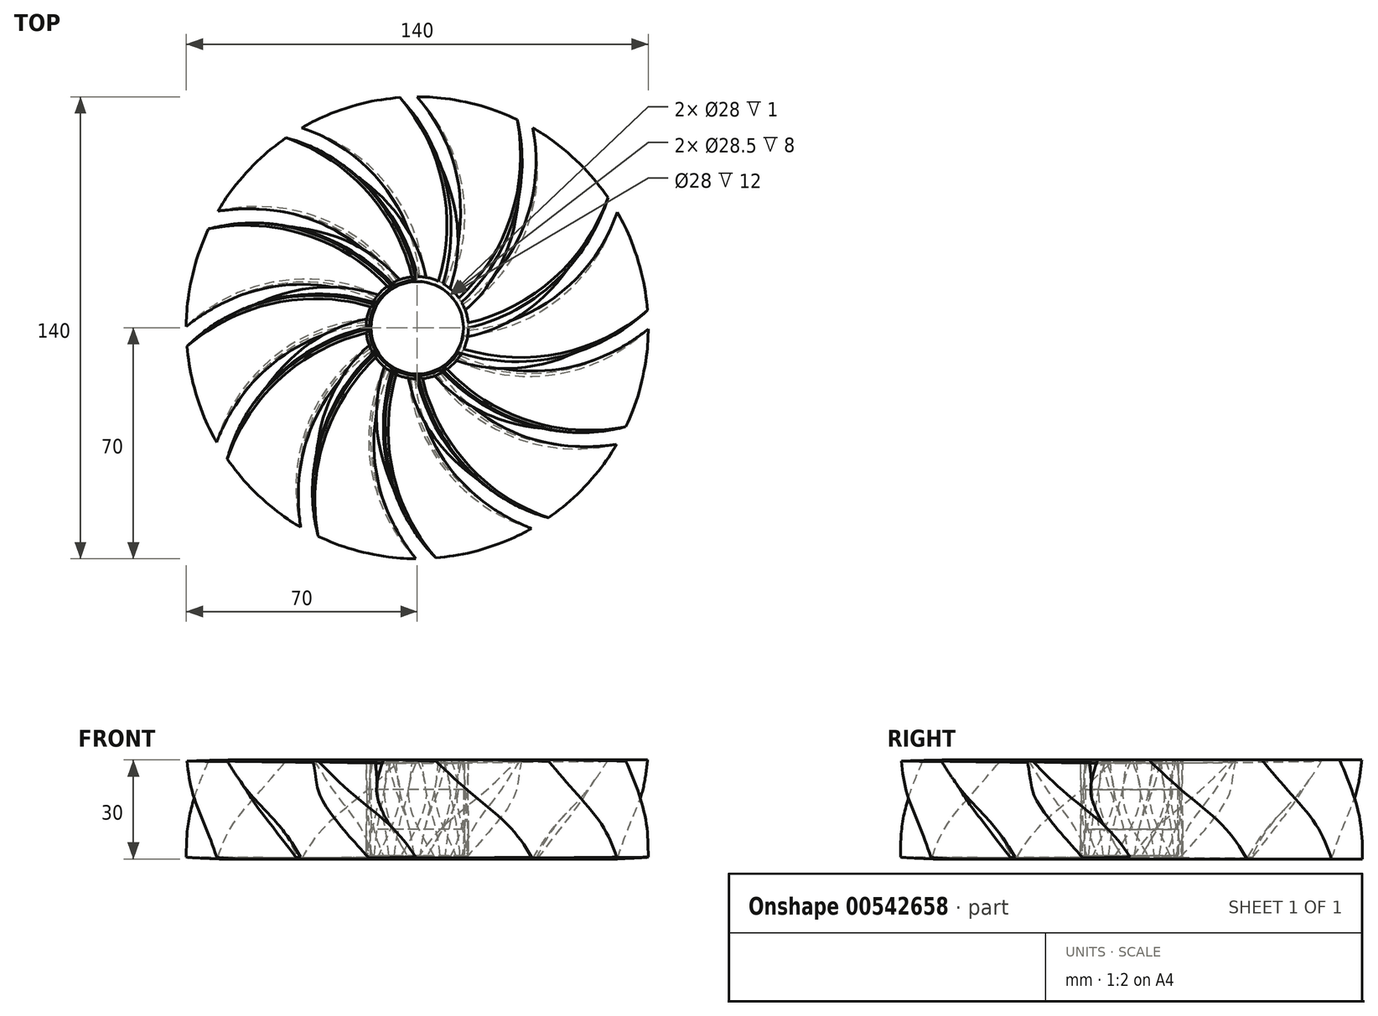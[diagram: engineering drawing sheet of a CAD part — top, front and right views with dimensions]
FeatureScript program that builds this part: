
annotation { "Feature Type Name" : "Feature", "Feature Type Description" : "" }
export const myFeature = defineFeature(function(context is Context, id is Id, definition is map)
    precondition{}
    {
        {
            var Q0;
            Q0=qCreatedBy(makeId("Top.planeOp"),FACE);
            var sketch = newSketch(context, id + "F0", { "sketchPlane" : qUnion([Q0])});
            skArc(sketch, "E0", {"start": v(0, 0) * mm, "mid": v(35, -13.15) * mm, "end": v(70, 0) * mm});
            skArc(sketch, "E1", {"start": v(0, -2) * mm, "mid": v(35.38, -14.4) * mm, "end": v(70, 0) * mm});
            skLineSegment(sketch, "E2", {"start": v(0, -2) * mm, "end": v(0, 0) * mm});
            skSolve(sketch);
        }
        {
            var Q0;
            Q0=qCreatedBy(makeId("Top.planeOp"),FACE);
            cPlane(context, id + "F1", {"entities" : qUnion([Q0]), "cplaneType" : CPlaneType.OFFSET, "offset" : 10 * mm, "width" : 150 * mm, "height" : 150 * mm});
        }
        {
            var Q0;
            Q0=qCreatedBy(id+"F1.planeOp",FACE);
            var sketch = newSketch(context, id + "F2", { "sketchPlane" : qUnion([Q0])});
            skArc(sketch, "E3", {"start": v(0, 0) * mm, "mid": v(33.25, -17.1) * mm, "end": v(69.54, -8.05) * mm});
            skArc(sketch, "E4", {"start": v(-0.44, -4.98) * mm, "mid": v(33.82, -23.17) * mm, "end": v(69.54, -8.05) * mm});
            skLineSegment(sketch, "E5", {"start": v(-0.44, -4.98) * mm, "end": v(0, 0) * mm});
            skSolve(sketch);
        }
        {
            var Q0;
            Q0=qCreatedBy(id+"F1.planeOp",FACE);
            cPlane(context, id + "F3", {"entities" : qUnion([Q0]), "cplaneType" : CPlaneType.OFFSET, "offset" : 10 * mm, "width" : 150 * mm, "height" : 150 * mm});
        }
        {
            var Q0;
            Q0=qCreatedBy(id+"F3.planeOp",FACE);
            var sketch = newSketch(context, id + "F4", { "sketchPlane" : qUnion([Q0])});
            skArc(sketch, "E6", {"start": v(0, 0) * mm, "mid": v(29.78, -22.6) * mm, "end": v(67.08, -20) * mm});
            skArc(sketch, "E7", {"start": v(-1.3, -4.83) * mm, "mid": v(29.28, -28.7) * mm, "end": v(67.08, -20) * mm});
            skLineSegment(sketch, "E8", {"start": v(-1.3, -4.83) * mm, "end": v(0, 0) * mm});
            skSolve(sketch);
        }
        {
            var Q0;
            Q0=qCreatedBy(id+"F3.planeOp",FACE);
            cPlane(context, id + "F5", {"entities" : qUnion([Q0]), "cplaneType" : CPlaneType.OFFSET, "offset" : 10 * mm, "width" : 150 * mm, "height" : 150 * mm});
        }
        {
            var Q0;
            Q0=qCreatedBy(id+"F5.planeOp",FACE);
            var sketch = newSketch(context, id + "F6", { "sketchPlane" : qUnion([Q0])});
            skArc(sketch, "E9", {"start": v(0, 0) * mm, "mid": v(26.56, -25.53) * mm, "end": v(63.1, -30.32) * mm});
            skArc(sketch, "E10", {"start": v(-0.85, -1.81) * mm, "mid": v(26.37, -26.72) * mm, "end": v(63.1, -30.32) * mm});
            skLineSegment(sketch, "E11", {"start": v(-0.85, -1.81) * mm, "end": v(0, 0) * mm});
            skSolve(sketch);
        }
        {
            var Q0;
            Q0=makeQuery(id+"F0.imprint","IMPRINT",FACE,{"disambiguationData":[TD([[makeQuery(id+"F0.imprint","IMPRINT",EDGE,{"derivedFrom":sQuery(id+"F0.wireOp",EDGE,"E0")}),-1.0]])]});
            var Q1;
            Q1=makeQuery(id+"F2.imprint","IMPRINT",FACE,{"disambiguationData":[TD([[makeQuery(id+"F2.imprint","IMPRINT",EDGE,{"derivedFrom":sQuery(id+"F2.wireOp",EDGE,"E3")}),-1.0]])]});
            var Q2;
            Q2=makeQuery(id+"F4.imprint","IMPRINT",FACE,{"disambiguationData":[TD([[makeQuery(id+"F4.imprint","IMPRINT",EDGE,{"derivedFrom":sQuery(id+"F4.wireOp",EDGE,"E6")}),-1.0]])]});
            var Q3;
            Q3=makeQuery(id+"F6.imprint","IMPRINT",FACE,{"disambiguationData":[TD([[makeQuery(id+"F6.imprint","IMPRINT",EDGE,{"derivedFrom":sQuery(id+"F6.wireOp",EDGE,"E9")}),-1.0]])]});
            loft(context, id + "F7", {"sheetProfilesArray" : [{ "sheetProfileEntities" : qUnion([Q0]) }, { "sheetProfileEntities" : qUnion([Q1]) }, { "sheetProfileEntities" : qUnion([Q2]) }, { "sheetProfileEntities" : qUnion([Q3]) }]});
        }
        {
            var Q0;
            Q0=qCreatedBy(makeId("Top.planeOp"),FACE);
            var sketch = newSketch(context, id + "F8", { "sketchPlane" : qUnion([Q0])});
            skLineSegment(sketch, "E12", {"start": v(0, 0) * mm, "end": v(-0.34, -0.76) * mm});
            skLineSegment(sketch, "E13", {"start": v(-0.34, -0.76) * mm, "end": v(0.32, -0.76) * mm});
            skLineSegment(sketch, "E14", {"start": v(0.32, -0.76) * mm, "end": v(0, 0) * mm});
            skSolve(sketch);
        }
        {
            var Q0;
            Q0 = qSketchRegion(id + "F8", true);
            extrude(context, id + "F9", {"entities" : qUnion([Q0]), "operationType" : NewBodyOperationType.ADD, "depth" : 40 * mm, "offsetDistance" : 25 * mm});
        }
        {
            var Q0;
            Q0=makeQuery(id+"F7.opLoft","SWEPT_BODY",BODY,{"disambiguationData":[OSD([makeQuery(id+"F0.imprint","IMPRINT",FACE,{"disambiguationData":[TD([[makeQuery(id+"F0.imprint","IMPRINT",EDGE,{"derivedFrom":sQuery(id+"F0.wireOp",EDGE,"E0")}),-1.0]])]}),sQuery(id+"F2.wireOp",EDGE,"E5"),sQuery(id+"F4.wireOp",EDGE,"E8"),makeQuery(id+"F6.imprint","IMPRINT",FACE,{"disambiguationData":[TD([[makeQuery(id+"F6.imprint","IMPRINT",EDGE,{"derivedFrom":sQuery(id+"F6.wireOp",EDGE,"E9")}),-1.0]])]})])]});
            var Q1;
            Q1=makeQuery(id+"F9.boolean.opBoolean","SPLIT",EDGE,{"derivedFrom":makeQuery(id+"F9.opExtrude","SWEPT_EDGE",EDGE,{"disambiguationData":[OSD([sQuery(id+"F8.wireOp",EDGE,"E12"),sQuery(id+"F8.wireOp",EDGE,"E14")])]})});
            circularPattern(context, id + "F10", {"entities" : qUnion([Q0]), "axis" : qUnion([Q1]), "angle" : 360 * degree, "instanceCount" : 12, "equalSpace" : true});
        }
        {
            var Q0;
            Q0=qCreatedBy(makeId("Top.planeOp"),FACE);
            var sketch = newSketch(context, id + "F11", { "sketchPlane" : qUnion([Q0])});
            skCircle(sketch, "E15", {"center": v(0, 0) * mm, "radius": 15.5 * mm});
            skSolve(sketch);
        }
        {
            var Q0;
            Q0 = qSketchRegion(id + "F11", true);
            extrude(context, id + "F12", {"entities" : qUnion([Q0]), "operationType" : NewBodyOperationType.ADD, "depth" : 30 * mm, "offsetDistance" : 25 * mm});
        }
        {
            var Q0;
            Q0=qCreatedBy(makeId("Top.planeOp"),FACE);
            var sketch = newSketch(context, id + "F13", { "sketchPlane" : qUnion([Q0])});
            skCircle(sketch, "E16", {"center": v(0, 0) * mm, "radius": 14 * mm});
            skSolve(sketch);
        }
        {
            var Q0;
            Q0 = qSketchRegion(id + "F13", true);
            extrude(context, id + "F14", {"entities" : qUnion([Q0]), "operationType" : NewBodyOperationType.REMOVE, "depth" : 40 * mm, "offsetDistance" : 25 * mm});
        }
        {
            var Q0;
            Q0=qCreatedBy(makeId("Top.planeOp"),FACE);
            var sketch = newSketch(context, id + "F15", { "sketchPlane" : qUnion([Q0])});
            skCircle(sketch, "E17", {"center": v(0, 0) * mm, "radius": 14.25 * mm});
            skSolve(sketch);
        }
        {
            var Q0;
            Q0 = qSketchRegion(id + "F15", true);
            extrude(context, id + "F16", {"entities" : qUnion([Q0]), "operationType" : NewBodyOperationType.REMOVE, "depth" : 9 * mm, "offsetDistance" : 25 * mm, "hasSecondDirection" : true, "secondDirectionOppositeDirection" : false, "secondDirectionDepth" : 1 * mm});
        }
        {
            var Q0;
            Q0 = qSketchRegion(id + "F15", true);
            extrude(context, id + "F17", {"entities" : qUnion([Q0]), "operationType" : NewBodyOperationType.REMOVE, "depth" : 29 * mm, "offsetDistance" : 25 * mm, "hasSecondDirection" : true, "secondDirectionOppositeDirection" : false, "secondDirectionDepth" : 21 * mm});
        }
        {
            var Q0;
            {var subQ0=sQuery(id+"F2.wireOp",EDGE,"E3");var subQ1=sQuery(id+"F2.wireOp",EDGE,"E4");var subQ2=makeQuery(id+"F2.imprint","INTERSECT",VERTEX,{"derivedFrom":[subQ0,subQ1]});var subQ3=sQuery(id+"F2.wireOp",EDGE,"E5");var subQ4=sQuery(id+"F0.wireOp",EDGE,"E0");var subQ5=sQuery(id+"F0.wireOp",EDGE,"E1");var subQ6=makeQuery(id+"F0.imprint","INTERSECT",VERTEX,{"derivedFrom":[subQ4,subQ5]});var subQ7=sQuery(id+"F0.wireOp",EDGE,"E2");var subQ10=sQuery(id+"F11.wireOp",EDGE,"E15");Q0=makeQuery(id+"F12.boolean.opBoolean","SPLIT",EDGE,{"disambiguationData":[TD([makeQuery(id+"F10.opPattern","COPY",FACE,{"derivedFrom":makeQuery(id+"F7.opLoft","SWEPT_FACE",FACE,{"disambiguationData":[OSD([subQ4,subQ5,subQ7,subQ0,subQ1,subQ3]),TDD([subQ6,makeQuery(id+"F0.imprint","INTERSECT",VERTEX,{"derivedFrom":[subQ5,subQ7]}),makeQuery(id+"F0.imprint","IMPRINT",EDGE,{"derivedFrom":subQ5}),subQ2,makeQuery(id+"F2.imprint","INTERSECT",VERTEX,{"derivedFrom":[subQ1,subQ3]}),makeQuery(id+"F2.imprint","IMPRINT",EDGE,{"derivedFrom":subQ1})])]}),"instanceName":"3"})])],"derivedFrom":makeQuery(id+"F12.opExtrude","CAP_EDGE",EDGE,{"disambiguationData":[OSD([subQ10])],"isStart":false})});}
            var Q1;
            {var subQ0=sQuery(id+"F2.wireOp",EDGE,"E3");var subQ1=sQuery(id+"F2.wireOp",EDGE,"E4");var subQ2=makeQuery(id+"F2.imprint","INTERSECT",VERTEX,{"derivedFrom":[subQ0,subQ1]});var subQ3=sQuery(id+"F2.wireOp",EDGE,"E5");var subQ4=sQuery(id+"F0.wireOp",EDGE,"E0");var subQ5=sQuery(id+"F0.wireOp",EDGE,"E1");var subQ6=makeQuery(id+"F0.imprint","INTERSECT",VERTEX,{"derivedFrom":[subQ4,subQ5]});var subQ7=sQuery(id+"F0.wireOp",EDGE,"E2");var subQ10=sQuery(id+"F11.wireOp",EDGE,"E15");Q1=makeQuery(id+"F12.boolean.opBoolean","SPLIT",EDGE,{"disambiguationData":[TD([makeQuery(id+"F10.opPattern","COPY",FACE,{"derivedFrom":makeQuery(id+"F7.opLoft","SWEPT_FACE",FACE,{"disambiguationData":[OSD([subQ4,subQ5,subQ7,subQ0,subQ1,subQ3]),TDD([subQ6,makeQuery(id+"F0.imprint","INTERSECT",VERTEX,{"derivedFrom":[subQ5,subQ7]}),makeQuery(id+"F0.imprint","IMPRINT",EDGE,{"derivedFrom":subQ5}),subQ2,makeQuery(id+"F2.imprint","INTERSECT",VERTEX,{"derivedFrom":[subQ1,subQ3]}),makeQuery(id+"F2.imprint","IMPRINT",EDGE,{"derivedFrom":subQ1})])]}),"instanceName":"4"})])],"derivedFrom":makeQuery(id+"F12.opExtrude","CAP_EDGE",EDGE,{"disambiguationData":[OSD([subQ10])],"isStart":false})});}
            var Q2;
            {var subQ0=sQuery(id+"F2.wireOp",EDGE,"E3");var subQ1=sQuery(id+"F2.wireOp",EDGE,"E4");var subQ2=makeQuery(id+"F2.imprint","INTERSECT",VERTEX,{"derivedFrom":[subQ0,subQ1]});var subQ3=sQuery(id+"F2.wireOp",EDGE,"E5");var subQ4=sQuery(id+"F0.wireOp",EDGE,"E0");var subQ5=sQuery(id+"F0.wireOp",EDGE,"E1");var subQ6=makeQuery(id+"F0.imprint","INTERSECT",VERTEX,{"derivedFrom":[subQ4,subQ5]});var subQ7=sQuery(id+"F0.wireOp",EDGE,"E2");var subQ10=sQuery(id+"F11.wireOp",EDGE,"E15");Q2=makeQuery(id+"F12.boolean.opBoolean","SPLIT",EDGE,{"disambiguationData":[TD([makeQuery(id+"F10.opPattern","COPY",FACE,{"derivedFrom":makeQuery(id+"F7.opLoft","SWEPT_FACE",FACE,{"disambiguationData":[OSD([subQ4,subQ5,subQ7,subQ0,subQ1,subQ3]),TDD([subQ6,makeQuery(id+"F0.imprint","INTERSECT",VERTEX,{"derivedFrom":[subQ5,subQ7]}),makeQuery(id+"F0.imprint","IMPRINT",EDGE,{"derivedFrom":subQ5}),subQ2,makeQuery(id+"F2.imprint","INTERSECT",VERTEX,{"derivedFrom":[subQ1,subQ3]}),makeQuery(id+"F2.imprint","IMPRINT",EDGE,{"derivedFrom":subQ1})])]}),"instanceName":"5"})])],"derivedFrom":makeQuery(id+"F12.opExtrude","CAP_EDGE",EDGE,{"disambiguationData":[OSD([subQ10])],"isStart":false})});}
            var Q3;
            {var subQ0=sQuery(id+"F2.wireOp",EDGE,"E3");var subQ1=sQuery(id+"F2.wireOp",EDGE,"E4");var subQ2=makeQuery(id+"F2.imprint","INTERSECT",VERTEX,{"derivedFrom":[subQ0,subQ1]});var subQ3=sQuery(id+"F2.wireOp",EDGE,"E5");var subQ4=sQuery(id+"F0.wireOp",EDGE,"E0");var subQ5=sQuery(id+"F0.wireOp",EDGE,"E1");var subQ6=makeQuery(id+"F0.imprint","INTERSECT",VERTEX,{"derivedFrom":[subQ4,subQ5]});var subQ7=sQuery(id+"F0.wireOp",EDGE,"E2");var subQ10=sQuery(id+"F11.wireOp",EDGE,"E15");Q3=makeQuery(id+"F12.boolean.opBoolean","SPLIT",EDGE,{"disambiguationData":[TD([makeQuery(id+"F10.opPattern","COPY",FACE,{"derivedFrom":makeQuery(id+"F7.opLoft","SWEPT_FACE",FACE,{"disambiguationData":[OSD([subQ4,subQ5,subQ7,subQ0,subQ1,subQ3]),TDD([subQ6,makeQuery(id+"F0.imprint","INTERSECT",VERTEX,{"derivedFrom":[subQ5,subQ7]}),makeQuery(id+"F0.imprint","IMPRINT",EDGE,{"derivedFrom":subQ5}),subQ2,makeQuery(id+"F2.imprint","INTERSECT",VERTEX,{"derivedFrom":[subQ1,subQ3]}),makeQuery(id+"F2.imprint","IMPRINT",EDGE,{"derivedFrom":subQ1})])]}),"instanceName":"6"})])],"derivedFrom":makeQuery(id+"F12.opExtrude","CAP_EDGE",EDGE,{"disambiguationData":[OSD([subQ10])],"isStart":false})});}
            var Q4;
            {var subQ0=sQuery(id+"F2.wireOp",EDGE,"E4");var subQ1=sQuery(id+"F2.wireOp",EDGE,"E5");var subQ2=sQuery(id+"F2.wireOp",EDGE,"E3");var subQ3=makeQuery(id+"F2.imprint","INTERSECT",VERTEX,{"derivedFrom":[subQ2,subQ0]});var subQ4=sQuery(id+"F0.wireOp",EDGE,"E1");var subQ5=sQuery(id+"F0.wireOp",EDGE,"E2");var subQ6=sQuery(id+"F0.wireOp",EDGE,"E0");var subQ7=makeQuery(id+"F0.imprint","INTERSECT",VERTEX,{"derivedFrom":[subQ6,subQ4]});var subQ10=sQuery(id+"F11.wireOp",EDGE,"E15");Q4=makeQuery(id+"F12.boolean.opBoolean","SPLIT",EDGE,{"disambiguationData":[TD([makeQuery(id+"F7.opLoft","SWEPT_FACE",FACE,{"disambiguationData":[OSD([subQ6,subQ4,subQ5,subQ2,subQ0,subQ1]),TDD([makeQuery(id+"F0.imprint","INTERSECT",VERTEX,{"derivedFrom":[subQ6,subQ5]}),subQ7,makeQuery(id+"F0.imprint","IMPRINT",EDGE,{"derivedFrom":subQ6}),makeQuery(id+"F2.imprint","INTERSECT",VERTEX,{"derivedFrom":[subQ2,subQ1]}),subQ3,makeQuery(id+"F2.imprint","IMPRINT",EDGE,{"derivedFrom":subQ2})])]})])],"derivedFrom":makeQuery(id+"F12.opExtrude","CAP_EDGE",EDGE,{"disambiguationData":[OSD([subQ10])],"isStart":false})});}
            var Q5;
            {var subQ0=sQuery(id+"F2.wireOp",EDGE,"E4");var subQ1=sQuery(id+"F2.wireOp",EDGE,"E5");var subQ2=sQuery(id+"F2.wireOp",EDGE,"E3");var subQ3=makeQuery(id+"F2.imprint","INTERSECT",VERTEX,{"derivedFrom":[subQ2,subQ0]});var subQ4=sQuery(id+"F0.wireOp",EDGE,"E1");var subQ5=sQuery(id+"F0.wireOp",EDGE,"E2");var subQ6=sQuery(id+"F0.wireOp",EDGE,"E0");var subQ7=makeQuery(id+"F0.imprint","INTERSECT",VERTEX,{"derivedFrom":[subQ6,subQ4]});var subQ10=sQuery(id+"F11.wireOp",EDGE,"E15");Q5=makeQuery(id+"F12.boolean.opBoolean","SPLIT",EDGE,{"disambiguationData":[TD([makeQuery(id+"F7.opLoft","SWEPT_FACE",FACE,{"disambiguationData":[OSD([subQ6,subQ4,subQ5,subQ2,subQ0,subQ1]),TDD([subQ7,makeQuery(id+"F0.imprint","INTERSECT",VERTEX,{"derivedFrom":[subQ4,subQ5]}),makeQuery(id+"F0.imprint","IMPRINT",EDGE,{"derivedFrom":subQ4}),subQ3,makeQuery(id+"F2.imprint","INTERSECT",VERTEX,{"derivedFrom":[subQ0,subQ1]}),makeQuery(id+"F2.imprint","IMPRINT",EDGE,{"derivedFrom":subQ0})])]})])],"derivedFrom":makeQuery(id+"F12.opExtrude","CAP_EDGE",EDGE,{"disambiguationData":[OSD([subQ10])],"isStart":false})});}
            var Q6;
            {var subQ2=sQuery(id+"F2.wireOp",EDGE,"E4");var subQ3=sQuery(id+"F2.wireOp",EDGE,"E5");var subQ4=sQuery(id+"F2.wireOp",EDGE,"E3");var subQ5=makeQuery(id+"F2.imprint","INTERSECT",VERTEX,{"derivedFrom":[subQ4,subQ2]});var subQ6=sQuery(id+"F0.wireOp",EDGE,"E1");var subQ7=sQuery(id+"F0.wireOp",EDGE,"E2");var subQ8=sQuery(id+"F0.wireOp",EDGE,"E0");var subQ9=makeQuery(id+"F0.imprint","INTERSECT",VERTEX,{"derivedFrom":[subQ8,subQ6]});var subQ10=sQuery(id+"F11.wireOp",EDGE,"E15");Q6=makeQuery(id+"F12.boolean.opBoolean","SPLIT",EDGE,{"disambiguationData":[TD([makeQuery(id+"F10.opPattern","COPY",FACE,{"derivedFrom":makeQuery(id+"F7.opLoft","SWEPT_FACE",FACE,{"disambiguationData":[OSD([subQ8,subQ6,subQ7,subQ4,subQ2,subQ3]),TDD([subQ9,makeQuery(id+"F0.imprint","INTERSECT",VERTEX,{"derivedFrom":[subQ6,subQ7]}),makeQuery(id+"F0.imprint","IMPRINT",EDGE,{"derivedFrom":subQ6}),subQ5,makeQuery(id+"F2.imprint","INTERSECT",VERTEX,{"derivedFrom":[subQ2,subQ3]}),makeQuery(id+"F2.imprint","IMPRINT",EDGE,{"derivedFrom":subQ2})])]}),"instanceName":"1"})])],"derivedFrom":makeQuery(id+"F12.opExtrude","CAP_EDGE",EDGE,{"disambiguationData":[OSD([subQ10])],"isStart":false})});}
            var Q7;
            {var subQ0=sQuery(id+"F2.wireOp",EDGE,"E3");var subQ1=sQuery(id+"F2.wireOp",EDGE,"E4");var subQ2=makeQuery(id+"F2.imprint","INTERSECT",VERTEX,{"derivedFrom":[subQ0,subQ1]});var subQ3=sQuery(id+"F2.wireOp",EDGE,"E5");var subQ4=sQuery(id+"F0.wireOp",EDGE,"E0");var subQ5=sQuery(id+"F0.wireOp",EDGE,"E1");var subQ6=makeQuery(id+"F0.imprint","INTERSECT",VERTEX,{"derivedFrom":[subQ4,subQ5]});var subQ7=sQuery(id+"F0.wireOp",EDGE,"E2");var subQ10=sQuery(id+"F11.wireOp",EDGE,"E15");Q7=makeQuery(id+"F12.boolean.opBoolean","SPLIT",EDGE,{"disambiguationData":[TD([makeQuery(id+"F10.opPattern","COPY",FACE,{"derivedFrom":makeQuery(id+"F7.opLoft","SWEPT_FACE",FACE,{"disambiguationData":[OSD([subQ4,subQ5,subQ7,subQ0,subQ1,subQ3]),TDD([subQ6,makeQuery(id+"F0.imprint","INTERSECT",VERTEX,{"derivedFrom":[subQ5,subQ7]}),makeQuery(id+"F0.imprint","IMPRINT",EDGE,{"derivedFrom":subQ5}),subQ2,makeQuery(id+"F2.imprint","INTERSECT",VERTEX,{"derivedFrom":[subQ1,subQ3]}),makeQuery(id+"F2.imprint","IMPRINT",EDGE,{"derivedFrom":subQ1})])]}),"instanceName":"2"})])],"derivedFrom":makeQuery(id+"F12.opExtrude","CAP_EDGE",EDGE,{"disambiguationData":[OSD([subQ10])],"isStart":false})});}
            var Q8;
            {var subQ0=sQuery(id+"F6.wireOp",EDGE,"E9");var subQ1=sQuery(id+"F6.wireOp",EDGE,"E10");var subQ2=sQuery(id+"F6.wireOp",EDGE,"E11");Q8=makeQuery(id+"F10.opPattern","COPY",EDGE,{"derivedFrom":makeQuery(id+"F7.opLoft","MID_CAP_EDGE",EDGE,{"disambiguationData":[OSD([subQ0,subQ1,subQ2]),TDD([makeQuery(id+"F6.imprint","INTERSECT",VERTEX,{"derivedFrom":[subQ0,subQ2]}),makeQuery(id+"F6.imprint","INTERSECT",VERTEX,{"derivedFrom":[subQ0,subQ1]}),makeQuery(id+"F6.imprint","IMPRINT",EDGE,{"derivedFrom":subQ0})])],"capPos":3.0}),"instanceName":"5"});}
            var Q9;
            {var subQ0=sQuery(id+"F6.wireOp",EDGE,"E9");var subQ1=sQuery(id+"F6.wireOp",EDGE,"E10");var subQ2=sQuery(id+"F6.wireOp",EDGE,"E11");Q9=makeQuery(id+"F10.opPattern","COPY",EDGE,{"derivedFrom":makeQuery(id+"F7.opLoft","MID_CAP_EDGE",EDGE,{"disambiguationData":[OSD([subQ0,subQ1,subQ2]),TDD([makeQuery(id+"F6.imprint","INTERSECT",VERTEX,{"derivedFrom":[subQ0,subQ2]}),makeQuery(id+"F6.imprint","INTERSECT",VERTEX,{"derivedFrom":[subQ0,subQ1]}),makeQuery(id+"F6.imprint","IMPRINT",EDGE,{"derivedFrom":subQ0})])],"capPos":3.0}),"instanceName":"4"});}
            var Q10;
            {var subQ0=sQuery(id+"F6.wireOp",EDGE,"E9");var subQ1=sQuery(id+"F6.wireOp",EDGE,"E10");var subQ2=sQuery(id+"F6.wireOp",EDGE,"E11");Q10=makeQuery(id+"F10.opPattern","COPY",EDGE,{"derivedFrom":makeQuery(id+"F7.opLoft","MID_CAP_EDGE",EDGE,{"disambiguationData":[OSD([subQ0,subQ1,subQ2]),TDD([makeQuery(id+"F6.imprint","INTERSECT",VERTEX,{"derivedFrom":[subQ0,subQ2]}),makeQuery(id+"F6.imprint","INTERSECT",VERTEX,{"derivedFrom":[subQ0,subQ1]}),makeQuery(id+"F6.imprint","IMPRINT",EDGE,{"derivedFrom":subQ0})])],"capPos":3.0}),"instanceName":"3"});}
            var Q11;
            {var subQ0=sQuery(id+"F6.wireOp",EDGE,"E9");var subQ1=sQuery(id+"F6.wireOp",EDGE,"E10");var subQ2=sQuery(id+"F6.wireOp",EDGE,"E11");Q11=makeQuery(id+"F10.opPattern","COPY",EDGE,{"derivedFrom":makeQuery(id+"F7.opLoft","MID_CAP_EDGE",EDGE,{"disambiguationData":[OSD([subQ0,subQ1,subQ2]),TDD([makeQuery(id+"F6.imprint","INTERSECT",VERTEX,{"derivedFrom":[subQ0,subQ2]}),makeQuery(id+"F6.imprint","INTERSECT",VERTEX,{"derivedFrom":[subQ0,subQ1]}),makeQuery(id+"F6.imprint","IMPRINT",EDGE,{"derivedFrom":subQ0})])],"capPos":3.0}),"instanceName":"2"});}
            var Q12;
            {var subQ0=sQuery(id+"F6.wireOp",EDGE,"E9");var subQ1=sQuery(id+"F6.wireOp",EDGE,"E10");var subQ2=sQuery(id+"F6.wireOp",EDGE,"E11");Q12=makeQuery(id+"F10.opPattern","COPY",EDGE,{"derivedFrom":makeQuery(id+"F7.opLoft","MID_CAP_EDGE",EDGE,{"disambiguationData":[OSD([subQ0,subQ1,subQ2]),TDD([makeQuery(id+"F6.imprint","INTERSECT",VERTEX,{"derivedFrom":[subQ0,subQ2]}),makeQuery(id+"F6.imprint","INTERSECT",VERTEX,{"derivedFrom":[subQ0,subQ1]}),makeQuery(id+"F6.imprint","IMPRINT",EDGE,{"derivedFrom":subQ0})])],"capPos":3.0}),"instanceName":"1"});}
            var Q13;
            {var subQ0=sQuery(id+"F6.wireOp",EDGE,"E9");var subQ1=sQuery(id+"F6.wireOp",EDGE,"E10");var subQ2=sQuery(id+"F6.wireOp",EDGE,"E11");Q13=makeQuery(id+"F7.opLoft","MID_CAP_EDGE",EDGE,{"disambiguationData":[OSD([subQ0,subQ1,subQ2]),TDD([makeQuery(id+"F6.imprint","INTERSECT",VERTEX,{"derivedFrom":[subQ0,subQ2]}),makeQuery(id+"F6.imprint","INTERSECT",VERTEX,{"derivedFrom":[subQ0,subQ1]}),makeQuery(id+"F6.imprint","IMPRINT",EDGE,{"derivedFrom":subQ0})])],"capPos":3.0});}
            var Q14;
            {var subQ0=sQuery(id+"F6.wireOp",EDGE,"E9");var subQ1=sQuery(id+"F6.wireOp",EDGE,"E10");var subQ2=sQuery(id+"F6.wireOp",EDGE,"E11");Q14=makeQuery(id+"F10.opPattern","COPY",EDGE,{"derivedFrom":makeQuery(id+"F7.opLoft","MID_CAP_EDGE",EDGE,{"disambiguationData":[OSD([subQ0,subQ1,subQ2]),TDD([makeQuery(id+"F6.imprint","INTERSECT",VERTEX,{"derivedFrom":[subQ0,subQ2]}),makeQuery(id+"F6.imprint","INTERSECT",VERTEX,{"derivedFrom":[subQ0,subQ1]}),makeQuery(id+"F6.imprint","IMPRINT",EDGE,{"derivedFrom":subQ0})])],"capPos":3.0}),"instanceName":"7"});}
            var Q15;
            {var subQ0=sQuery(id+"F6.wireOp",EDGE,"E9");var subQ1=sQuery(id+"F6.wireOp",EDGE,"E10");var subQ2=sQuery(id+"F6.wireOp",EDGE,"E11");Q15=makeQuery(id+"F10.opPattern","COPY",EDGE,{"derivedFrom":makeQuery(id+"F7.opLoft","MID_CAP_EDGE",EDGE,{"disambiguationData":[OSD([subQ0,subQ1,subQ2]),TDD([makeQuery(id+"F6.imprint","INTERSECT",VERTEX,{"derivedFrom":[subQ0,subQ2]}),makeQuery(id+"F6.imprint","INTERSECT",VERTEX,{"derivedFrom":[subQ0,subQ1]}),makeQuery(id+"F6.imprint","IMPRINT",EDGE,{"derivedFrom":subQ0})])],"capPos":3.0}),"instanceName":"6"});}
            chamfer(context, id + "F18", {"entities" : qUnion([Q0, Q1, Q2, Q3, Q4, Q5, Q6, Q7, Q8, Q9, Q10, Q11, Q12, Q13, Q14, Q15]), "width" : 1 * mm, "tangentPropagation" : true});
        }
        {
            var Q0;
            {var subQ0=sQuery(id+"F2.wireOp",EDGE,"E3");var subQ1=sQuery(id+"F2.wireOp",EDGE,"E4");var subQ2=makeQuery(id+"F2.imprint","INTERSECT",VERTEX,{"derivedFrom":[subQ0,subQ1]});var subQ3=sQuery(id+"F2.wireOp",EDGE,"E5");var subQ4=sQuery(id+"F0.wireOp",EDGE,"E0");var subQ6=sQuery(id+"F0.wireOp",EDGE,"E1");var subQ7=makeQuery(id+"F0.imprint","INTERSECT",VERTEX,{"derivedFrom":[subQ4,subQ6]});var subQ8=sQuery(id+"F0.wireOp",EDGE,"E2");var subQ9=makeQuery(id+"F0.imprint","IMPRINT",EDGE,{"derivedFrom":subQ6});var subQ11=sQuery(id+"F11.wireOp",EDGE,"E15");Q0=makeQuery(id+"F12.boolean.opBoolean","SPLIT",EDGE,{"disambiguationData":[TD([makeQuery(id+"F10.opPattern","COPY",FACE,{"derivedFrom":makeQuery(id+"F7.opLoft","SWEPT_FACE",FACE,{"disambiguationData":[OSD([subQ4,subQ6,subQ8,subQ0,subQ1,subQ3]),TDD([subQ7,makeQuery(id+"F0.imprint","INTERSECT",VERTEX,{"derivedFrom":[subQ6,subQ8]}),subQ9,subQ2,makeQuery(id+"F2.imprint","INTERSECT",VERTEX,{"derivedFrom":[subQ1,subQ3]}),makeQuery(id+"F2.imprint","IMPRINT",EDGE,{"derivedFrom":subQ1})])]}),"instanceName":"5"})])],"derivedFrom":makeQuery(id+"F12.opExtrude","CAP_EDGE",EDGE,{"disambiguationData":[OSD([subQ11])],"isStart":true})});}
            var Q1;
            {var subQ0=sQuery(id+"F0.wireOp",EDGE,"E1");var subQ1=sQuery(id+"F0.wireOp",EDGE,"E2");var subQ2=sQuery(id+"F0.wireOp",EDGE,"E0");Q1=makeQuery(id+"F10.opPattern","COPY",EDGE,{"derivedFrom":makeQuery(id+"F7.opLoft","MID_CAP_EDGE",EDGE,{"disambiguationData":[OSD([subQ2,subQ0,subQ1]),TDD([makeQuery(id+"F0.imprint","INTERSECT",VERTEX,{"derivedFrom":[subQ2,subQ0]}),makeQuery(id+"F0.imprint","INTERSECT",VERTEX,{"derivedFrom":[subQ0,subQ1]}),makeQuery(id+"F0.imprint","IMPRINT",EDGE,{"derivedFrom":subQ0})])],"capPos":0.0}),"instanceName":"6"});}
            var Q2;
            {var subQ0=sQuery(id+"F2.wireOp",EDGE,"E3");var subQ1=sQuery(id+"F2.wireOp",EDGE,"E4");var subQ2=makeQuery(id+"F2.imprint","INTERSECT",VERTEX,{"derivedFrom":[subQ0,subQ1]});var subQ3=sQuery(id+"F2.wireOp",EDGE,"E5");var subQ4=sQuery(id+"F0.wireOp",EDGE,"E0");var subQ6=sQuery(id+"F0.wireOp",EDGE,"E1");var subQ7=makeQuery(id+"F0.imprint","INTERSECT",VERTEX,{"derivedFrom":[subQ4,subQ6]});var subQ8=sQuery(id+"F0.wireOp",EDGE,"E2");var subQ9=makeQuery(id+"F0.imprint","IMPRINT",EDGE,{"derivedFrom":subQ6});var subQ11=sQuery(id+"F11.wireOp",EDGE,"E15");Q2=makeQuery(id+"F12.boolean.opBoolean","SPLIT",EDGE,{"disambiguationData":[TD([makeQuery(id+"F10.opPattern","COPY",FACE,{"derivedFrom":makeQuery(id+"F7.opLoft","SWEPT_FACE",FACE,{"disambiguationData":[OSD([subQ4,subQ6,subQ8,subQ0,subQ1,subQ3]),TDD([subQ7,makeQuery(id+"F0.imprint","INTERSECT",VERTEX,{"derivedFrom":[subQ6,subQ8]}),subQ9,subQ2,makeQuery(id+"F2.imprint","INTERSECT",VERTEX,{"derivedFrom":[subQ1,subQ3]}),makeQuery(id+"F2.imprint","IMPRINT",EDGE,{"derivedFrom":subQ1})])]}),"instanceName":"6"})])],"derivedFrom":makeQuery(id+"F12.opExtrude","CAP_EDGE",EDGE,{"disambiguationData":[OSD([subQ11])],"isStart":true})});}
            var Q3;
            {var subQ0=sQuery(id+"F0.wireOp",EDGE,"E1");var subQ1=sQuery(id+"F0.wireOp",EDGE,"E2");var subQ2=sQuery(id+"F0.wireOp",EDGE,"E0");Q3=makeQuery(id+"F10.opPattern","COPY",EDGE,{"derivedFrom":makeQuery(id+"F7.opLoft","MID_CAP_EDGE",EDGE,{"disambiguationData":[OSD([subQ2,subQ0,subQ1]),TDD([makeQuery(id+"F0.imprint","INTERSECT",VERTEX,{"derivedFrom":[subQ2,subQ0]}),makeQuery(id+"F0.imprint","INTERSECT",VERTEX,{"derivedFrom":[subQ0,subQ1]}),makeQuery(id+"F0.imprint","IMPRINT",EDGE,{"derivedFrom":subQ0})])],"capPos":0.0}),"instanceName":"7"});}
            var Q4;
            {var subQ0=sQuery(id+"F2.wireOp",EDGE,"E4");var subQ1=sQuery(id+"F2.wireOp",EDGE,"E5");var subQ2=sQuery(id+"F2.wireOp",EDGE,"E3");var subQ3=makeQuery(id+"F2.imprint","INTERSECT",VERTEX,{"derivedFrom":[subQ2,subQ0]});var subQ4=sQuery(id+"F0.wireOp",EDGE,"E1");var subQ6=sQuery(id+"F0.wireOp",EDGE,"E2");var subQ7=sQuery(id+"F0.wireOp",EDGE,"E0");var subQ8=makeQuery(id+"F0.imprint","INTERSECT",VERTEX,{"derivedFrom":[subQ7,subQ4]});var subQ9=makeQuery(id+"F0.imprint","IMPRINT",EDGE,{"derivedFrom":subQ7});var subQ13=sQuery(id+"F11.wireOp",EDGE,"E15");Q4=makeQuery(id+"F12.boolean.opBoolean","SPLIT",EDGE,{"disambiguationData":[TD([makeQuery(id+"F7.opLoft","SWEPT_FACE",FACE,{"disambiguationData":[OSD([subQ7,subQ4,subQ6,subQ2,subQ0,subQ1]),TDD([makeQuery(id+"F0.imprint","INTERSECT",VERTEX,{"derivedFrom":[subQ7,subQ6]}),subQ8,subQ9,makeQuery(id+"F2.imprint","INTERSECT",VERTEX,{"derivedFrom":[subQ2,subQ1]}),subQ3,makeQuery(id+"F2.imprint","IMPRINT",EDGE,{"derivedFrom":subQ2})])]})])],"derivedFrom":makeQuery(id+"F12.opExtrude","CAP_EDGE",EDGE,{"disambiguationData":[OSD([subQ13])],"isStart":true})});}
            var Q5;
            {var subQ0=sQuery(id+"F0.wireOp",EDGE,"E1");var subQ1=sQuery(id+"F0.wireOp",EDGE,"E2");var subQ2=sQuery(id+"F0.wireOp",EDGE,"E0");Q5=makeQuery(id+"F7.opLoft","MID_CAP_EDGE",EDGE,{"disambiguationData":[OSD([subQ2,subQ0,subQ1]),TDD([makeQuery(id+"F0.imprint","INTERSECT",VERTEX,{"derivedFrom":[subQ2,subQ0]}),makeQuery(id+"F0.imprint","INTERSECT",VERTEX,{"derivedFrom":[subQ0,subQ1]}),makeQuery(id+"F0.imprint","IMPRINT",EDGE,{"derivedFrom":subQ0})])],"capPos":0.0});}
            var Q6;
            {var subQ1=sQuery(id+"F0.wireOp",EDGE,"E0");var subQ3=sQuery(id+"F0.wireOp",EDGE,"E1");var subQ4=makeQuery(id+"F0.imprint","IMPRINT",EDGE,{"derivedFrom":subQ3});var subQ5=sQuery(id+"F0.wireOp",EDGE,"E2");var subQ8=sQuery(id+"F2.wireOp",EDGE,"E4");var subQ9=sQuery(id+"F2.wireOp",EDGE,"E5");var subQ10=sQuery(id+"F2.wireOp",EDGE,"E3");var subQ11=makeQuery(id+"F2.imprint","INTERSECT",VERTEX,{"derivedFrom":[subQ10,subQ8]});var subQ12=makeQuery(id+"F0.imprint","INTERSECT",VERTEX,{"derivedFrom":[subQ1,subQ3]});var subQ13=sQuery(id+"F11.wireOp",EDGE,"E15");Q6=makeQuery(id+"F12.boolean.opBoolean","SPLIT",EDGE,{"disambiguationData":[TD([makeQuery(id+"F7.opLoft","SWEPT_FACE",FACE,{"disambiguationData":[OSD([subQ1,subQ3,subQ5,subQ10,subQ8,subQ9]),TDD([subQ12,makeQuery(id+"F0.imprint","INTERSECT",VERTEX,{"derivedFrom":[subQ3,subQ5]}),subQ4,subQ11,makeQuery(id+"F2.imprint","INTERSECT",VERTEX,{"derivedFrom":[subQ8,subQ9]}),makeQuery(id+"F2.imprint","IMPRINT",EDGE,{"derivedFrom":subQ8})])]})])],"derivedFrom":makeQuery(id+"F12.opExtrude","CAP_EDGE",EDGE,{"disambiguationData":[OSD([subQ13])],"isStart":true})});}
            var Q7;
            {var subQ0=sQuery(id+"F0.wireOp",EDGE,"E1");var subQ1=sQuery(id+"F0.wireOp",EDGE,"E2");var subQ2=sQuery(id+"F0.wireOp",EDGE,"E0");Q7=makeQuery(id+"F10.opPattern","COPY",EDGE,{"derivedFrom":makeQuery(id+"F7.opLoft","MID_CAP_EDGE",EDGE,{"disambiguationData":[OSD([subQ2,subQ0,subQ1]),TDD([makeQuery(id+"F0.imprint","INTERSECT",VERTEX,{"derivedFrom":[subQ2,subQ0]}),makeQuery(id+"F0.imprint","INTERSECT",VERTEX,{"derivedFrom":[subQ0,subQ1]}),makeQuery(id+"F0.imprint","IMPRINT",EDGE,{"derivedFrom":subQ0})])],"capPos":0.0}),"instanceName":"1"});}
            var Q8;
            {var subQ0=sQuery(id+"F2.wireOp",EDGE,"E3");var subQ1=sQuery(id+"F2.wireOp",EDGE,"E4");var subQ2=makeQuery(id+"F2.imprint","INTERSECT",VERTEX,{"derivedFrom":[subQ0,subQ1]});var subQ3=sQuery(id+"F2.wireOp",EDGE,"E5");var subQ4=sQuery(id+"F0.wireOp",EDGE,"E0");var subQ6=sQuery(id+"F0.wireOp",EDGE,"E1");var subQ7=makeQuery(id+"F0.imprint","INTERSECT",VERTEX,{"derivedFrom":[subQ4,subQ6]});var subQ8=sQuery(id+"F0.wireOp",EDGE,"E2");var subQ9=makeQuery(id+"F0.imprint","IMPRINT",EDGE,{"derivedFrom":subQ6});var subQ11=sQuery(id+"F11.wireOp",EDGE,"E15");Q8=makeQuery(id+"F12.boolean.opBoolean","SPLIT",EDGE,{"disambiguationData":[TD([makeQuery(id+"F10.opPattern","COPY",FACE,{"derivedFrom":makeQuery(id+"F7.opLoft","SWEPT_FACE",FACE,{"disambiguationData":[OSD([subQ4,subQ6,subQ8,subQ0,subQ1,subQ3]),TDD([subQ7,makeQuery(id+"F0.imprint","INTERSECT",VERTEX,{"derivedFrom":[subQ6,subQ8]}),subQ9,subQ2,makeQuery(id+"F2.imprint","INTERSECT",VERTEX,{"derivedFrom":[subQ1,subQ3]}),makeQuery(id+"F2.imprint","IMPRINT",EDGE,{"derivedFrom":subQ1})])]}),"instanceName":"1"})])],"derivedFrom":makeQuery(id+"F12.opExtrude","CAP_EDGE",EDGE,{"disambiguationData":[OSD([subQ11])],"isStart":true})});}
            var Q9;
            {var subQ0=sQuery(id+"F0.wireOp",EDGE,"E1");var subQ1=sQuery(id+"F0.wireOp",EDGE,"E2");var subQ2=sQuery(id+"F0.wireOp",EDGE,"E0");Q9=makeQuery(id+"F10.opPattern","COPY",EDGE,{"derivedFrom":makeQuery(id+"F7.opLoft","MID_CAP_EDGE",EDGE,{"disambiguationData":[OSD([subQ2,subQ0,subQ1]),TDD([makeQuery(id+"F0.imprint","INTERSECT",VERTEX,{"derivedFrom":[subQ2,subQ0]}),makeQuery(id+"F0.imprint","INTERSECT",VERTEX,{"derivedFrom":[subQ0,subQ1]}),makeQuery(id+"F0.imprint","IMPRINT",EDGE,{"derivedFrom":subQ0})])],"capPos":0.0}),"instanceName":"2"});}
            var Q10;
            {var subQ0=sQuery(id+"F2.wireOp",EDGE,"E3");var subQ1=sQuery(id+"F2.wireOp",EDGE,"E4");var subQ2=makeQuery(id+"F2.imprint","INTERSECT",VERTEX,{"derivedFrom":[subQ0,subQ1]});var subQ3=sQuery(id+"F2.wireOp",EDGE,"E5");var subQ4=sQuery(id+"F0.wireOp",EDGE,"E0");var subQ6=sQuery(id+"F0.wireOp",EDGE,"E1");var subQ7=makeQuery(id+"F0.imprint","INTERSECT",VERTEX,{"derivedFrom":[subQ4,subQ6]});var subQ8=sQuery(id+"F0.wireOp",EDGE,"E2");var subQ9=makeQuery(id+"F0.imprint","IMPRINT",EDGE,{"derivedFrom":subQ6});var subQ11=sQuery(id+"F11.wireOp",EDGE,"E15");Q10=makeQuery(id+"F12.boolean.opBoolean","SPLIT",EDGE,{"disambiguationData":[TD([makeQuery(id+"F10.opPattern","COPY",FACE,{"derivedFrom":makeQuery(id+"F7.opLoft","SWEPT_FACE",FACE,{"disambiguationData":[OSD([subQ4,subQ6,subQ8,subQ0,subQ1,subQ3]),TDD([subQ7,makeQuery(id+"F0.imprint","INTERSECT",VERTEX,{"derivedFrom":[subQ6,subQ8]}),subQ9,subQ2,makeQuery(id+"F2.imprint","INTERSECT",VERTEX,{"derivedFrom":[subQ1,subQ3]}),makeQuery(id+"F2.imprint","IMPRINT",EDGE,{"derivedFrom":subQ1})])]}),"instanceName":"2"})])],"derivedFrom":makeQuery(id+"F12.opExtrude","CAP_EDGE",EDGE,{"disambiguationData":[OSD([subQ11])],"isStart":true})});}
            var Q11;
            {var subQ0=sQuery(id+"F0.wireOp",EDGE,"E1");var subQ1=sQuery(id+"F0.wireOp",EDGE,"E2");var subQ2=sQuery(id+"F0.wireOp",EDGE,"E0");Q11=makeQuery(id+"F10.opPattern","COPY",EDGE,{"derivedFrom":makeQuery(id+"F7.opLoft","MID_CAP_EDGE",EDGE,{"disambiguationData":[OSD([subQ2,subQ0,subQ1]),TDD([makeQuery(id+"F0.imprint","INTERSECT",VERTEX,{"derivedFrom":[subQ2,subQ0]}),makeQuery(id+"F0.imprint","INTERSECT",VERTEX,{"derivedFrom":[subQ0,subQ1]}),makeQuery(id+"F0.imprint","IMPRINT",EDGE,{"derivedFrom":subQ0})])],"capPos":0.0}),"instanceName":"3"});}
            var Q12;
            {var subQ0=sQuery(id+"F2.wireOp",EDGE,"E3");var subQ1=sQuery(id+"F2.wireOp",EDGE,"E4");var subQ2=makeQuery(id+"F2.imprint","INTERSECT",VERTEX,{"derivedFrom":[subQ0,subQ1]});var subQ3=sQuery(id+"F2.wireOp",EDGE,"E5");var subQ4=sQuery(id+"F0.wireOp",EDGE,"E0");var subQ6=sQuery(id+"F0.wireOp",EDGE,"E1");var subQ7=makeQuery(id+"F0.imprint","INTERSECT",VERTEX,{"derivedFrom":[subQ4,subQ6]});var subQ8=sQuery(id+"F0.wireOp",EDGE,"E2");var subQ9=makeQuery(id+"F0.imprint","IMPRINT",EDGE,{"derivedFrom":subQ6});var subQ13=sQuery(id+"F11.wireOp",EDGE,"E15");Q12=makeQuery(id+"F12.boolean.opBoolean","SPLIT",EDGE,{"disambiguationData":[TD([makeQuery(id+"F10.opPattern","COPY",FACE,{"derivedFrom":makeQuery(id+"F7.opLoft","SWEPT_FACE",FACE,{"disambiguationData":[OSD([subQ4,subQ6,subQ8,subQ0,subQ1,subQ3]),TDD([subQ7,makeQuery(id+"F0.imprint","INTERSECT",VERTEX,{"derivedFrom":[subQ6,subQ8]}),subQ9,subQ2,makeQuery(id+"F2.imprint","INTERSECT",VERTEX,{"derivedFrom":[subQ1,subQ3]}),makeQuery(id+"F2.imprint","IMPRINT",EDGE,{"derivedFrom":subQ1})])]}),"instanceName":"3"})])],"derivedFrom":makeQuery(id+"F12.opExtrude","CAP_EDGE",EDGE,{"disambiguationData":[OSD([subQ13])],"isStart":true})});}
            var Q13;
            {var subQ0=sQuery(id+"F0.wireOp",EDGE,"E1");var subQ1=sQuery(id+"F0.wireOp",EDGE,"E2");var subQ2=sQuery(id+"F0.wireOp",EDGE,"E0");Q13=makeQuery(id+"F10.opPattern","COPY",EDGE,{"derivedFrom":makeQuery(id+"F7.opLoft","MID_CAP_EDGE",EDGE,{"disambiguationData":[OSD([subQ2,subQ0,subQ1]),TDD([makeQuery(id+"F0.imprint","INTERSECT",VERTEX,{"derivedFrom":[subQ2,subQ0]}),makeQuery(id+"F0.imprint","INTERSECT",VERTEX,{"derivedFrom":[subQ0,subQ1]}),makeQuery(id+"F0.imprint","IMPRINT",EDGE,{"derivedFrom":subQ0})])],"capPos":0.0}),"instanceName":"4"});}
            var Q14;
            {var subQ0=sQuery(id+"F2.wireOp",EDGE,"E3");var subQ1=sQuery(id+"F2.wireOp",EDGE,"E4");var subQ2=makeQuery(id+"F2.imprint","INTERSECT",VERTEX,{"derivedFrom":[subQ0,subQ1]});var subQ3=sQuery(id+"F2.wireOp",EDGE,"E5");var subQ4=sQuery(id+"F0.wireOp",EDGE,"E0");var subQ6=sQuery(id+"F0.wireOp",EDGE,"E1");var subQ7=makeQuery(id+"F0.imprint","INTERSECT",VERTEX,{"derivedFrom":[subQ4,subQ6]});var subQ8=sQuery(id+"F0.wireOp",EDGE,"E2");var subQ9=makeQuery(id+"F0.imprint","IMPRINT",EDGE,{"derivedFrom":subQ6});var subQ11=sQuery(id+"F11.wireOp",EDGE,"E15");Q14=makeQuery(id+"F12.boolean.opBoolean","SPLIT",EDGE,{"disambiguationData":[TD([makeQuery(id+"F10.opPattern","COPY",FACE,{"derivedFrom":makeQuery(id+"F7.opLoft","SWEPT_FACE",FACE,{"disambiguationData":[OSD([subQ4,subQ6,subQ8,subQ0,subQ1,subQ3]),TDD([subQ7,makeQuery(id+"F0.imprint","INTERSECT",VERTEX,{"derivedFrom":[subQ6,subQ8]}),subQ9,subQ2,makeQuery(id+"F2.imprint","INTERSECT",VERTEX,{"derivedFrom":[subQ1,subQ3]}),makeQuery(id+"F2.imprint","IMPRINT",EDGE,{"derivedFrom":subQ1})])]}),"instanceName":"4"})])],"derivedFrom":makeQuery(id+"F12.opExtrude","CAP_EDGE",EDGE,{"disambiguationData":[OSD([subQ11])],"isStart":true})});}
            var Q15;
            {var subQ0=sQuery(id+"F0.wireOp",EDGE,"E1");var subQ1=sQuery(id+"F0.wireOp",EDGE,"E2");var subQ2=sQuery(id+"F0.wireOp",EDGE,"E0");Q15=makeQuery(id+"F10.opPattern","COPY",EDGE,{"derivedFrom":makeQuery(id+"F7.opLoft","MID_CAP_EDGE",EDGE,{"disambiguationData":[OSD([subQ2,subQ0,subQ1]),TDD([makeQuery(id+"F0.imprint","INTERSECT",VERTEX,{"derivedFrom":[subQ2,subQ0]}),makeQuery(id+"F0.imprint","INTERSECT",VERTEX,{"derivedFrom":[subQ0,subQ1]}),makeQuery(id+"F0.imprint","IMPRINT",EDGE,{"derivedFrom":subQ0})])],"capPos":0.0}),"instanceName":"5"});}
            chamfer(context, id + "F19", {"entities" : qUnion([Q0, Q1, Q2, Q3, Q4, Q5, Q6, Q7, Q8, Q9, Q10, Q11, Q12, Q13, Q14, Q15]), "width" : 1 * mm, "tangentPropagation" : true});
        }
    });
